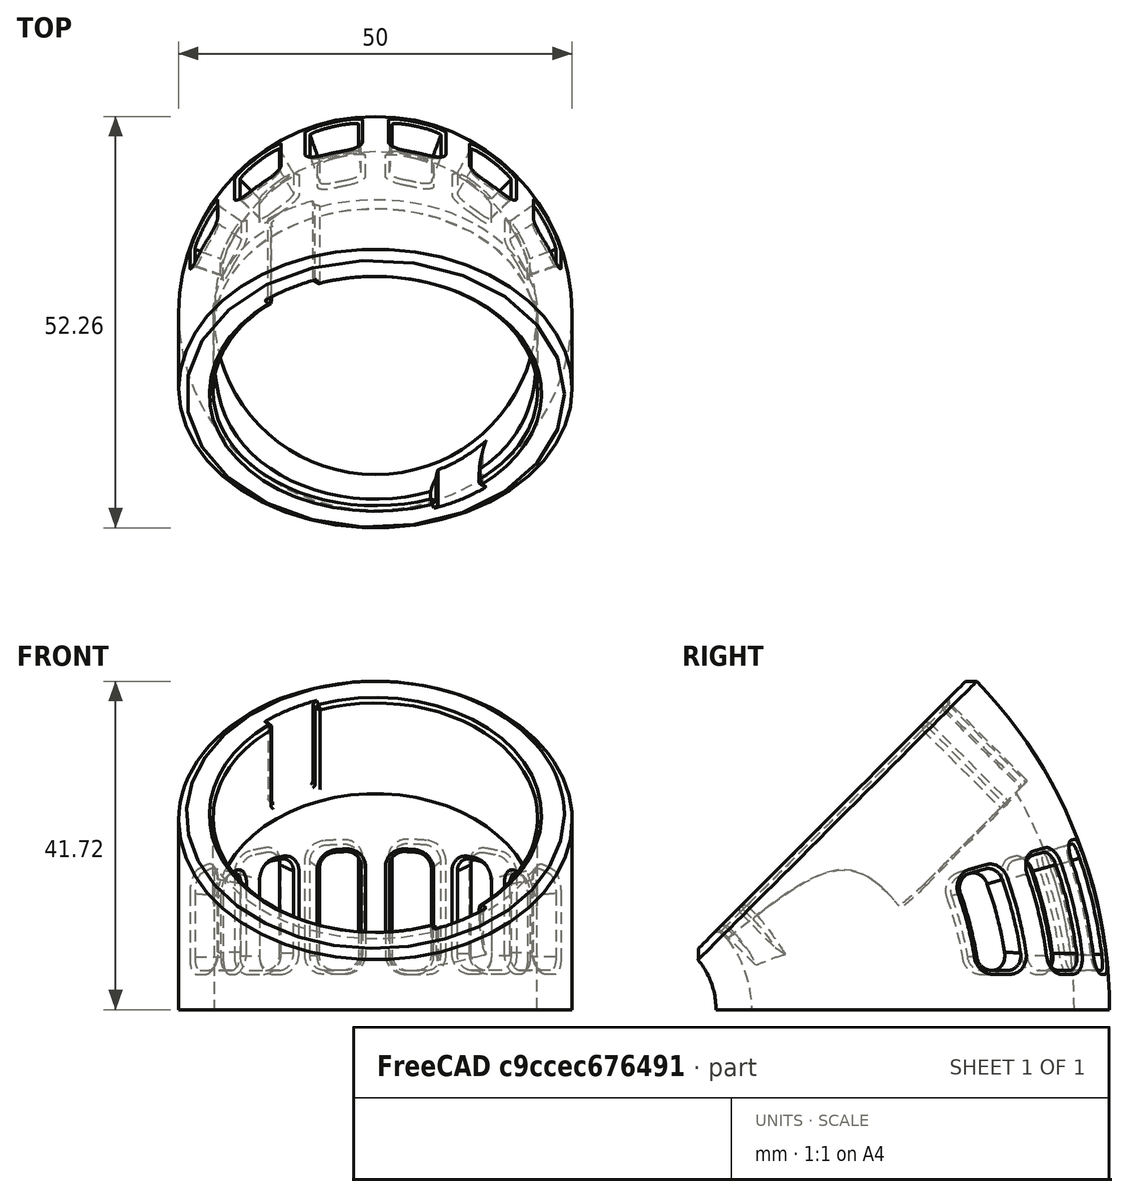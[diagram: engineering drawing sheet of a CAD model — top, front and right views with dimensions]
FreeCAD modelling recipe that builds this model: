
FCSTD DOCUMENT  (FreeCAD 0.19R18219 (Git))
Label: Hygrometerhalter-2
License: All rights reserved
LicenseURL: http://de.wikipedia.org/wiki/Alle_Rechte_vorbehalten
objects: Sketcher::SketchObject×3, PartDesign::Chamfer×3, PartDesign::Fillet×2, PartDesign::Line×1, PartDesign::Revolution×1, PartDesign::Pocket×1, PartDesign::Groove×1, PartDesign::Mirrored×1, PartDesign::Body×1, Mesh::Feature×1
note: 17 computed .brp shape members not serialized (recipe doc carries the construction recipe); baked Part::Feature solids carry a one-line shape summary decoded from their .brp

FEATURE [Sketcher::SketchObject] Sketch
  MapMode = 5
  Support = -> [XY_Plane]
  expr: Constraints[3] = 41mm
  sketch-geometry (2):
    g0: Circle CenterX=0 CenterY=0 CenterZ=0 NormalX=0 NormalY=0 NormalZ=1 AngleXU=0 Radius=25
    g1: Circle CenterX=0 CenterY=0 CenterZ=0 NormalX=0 NormalY=0 NormalZ=1 AngleXU=0 Radius=20.5
  constraints (4):
    c: Coincident(g0,g-1)
    c: Diameter(g0) = 50  'diameter'
    c: Coincident(g1,g0)
    c: Diameter(g1) = 41
FEATURE [PartDesign::Line] DatumLine
  AttacherType = Attacher::AttachEngineLine
  AttachmentOffset = pos=(-35,0,0) rot=(0,0,1;0rad)
  MapMode = 29
  Placement = pos=(0,-35,0) rot=(0.57735,0.57735,0.57735;2.0944rad)
  Support = -> [X_Axis]
FEATURE [PartDesign::Revolution] Revolution  label="Grundkörper"
  Angle = 45
  Axis = (1,0,0)
  Base = (0,-35,0)
  Profile = -> Sketch
  ReferenceAxis = -> DatumLine
  Refine = true
FEATURE [Sketcher::SketchObject] Sketch001
  ExternalGeometry = -> [Revolution]
  MapMode = 5
  Placement = pos=(0,-17.5,17.5) rot=(1,0,0;0.785398rad)
  Support = -> [Revolution]
  sketch-geometry (9):
    g0: ArcOfCircle CenterX=0 CenterY=10.2513 CenterZ=0 NormalX=0 NormalY=0 NormalZ=1 AngleXU=0 Radius=20.6 StartAngle=5.3876 EndAngle=8.22597
    g1: ArcOfCircle CenterX=0 CenterY=10.2513 CenterZ=0 NormalX=0 NormalY=0 NormalZ=1 AngleXU=0 Radius=20.6 StartAngle=2.246 EndAngle=5.08438
    g2: LineSegment StartX=-7.48746 StartY=29.4424 StartZ=0 EndX=-7.9418 EndY=30.6069 EndZ=0
    g3: ArcOfCircle CenterX=0 CenterY=10.2513 CenterZ=0 NormalX=0 NormalY=0 NormalZ=1 AngleXU=0 Radius=21.85 StartAngle=1.94279 EndAngle=2.246
    g4: LineSegment StartX=-13.6576 StartY=27.3069 StartZ=0 EndX=-12.8762 EndY=26.3311 EndZ=0
    g5: LineSegment StartX=12.8762 StartY=-5.82861 StartZ=0 EndX=13.6576 EndY=-6.80433 EndZ=0
    g6: LineSegment StartX=7.48746 StartY=-8.93983 StartZ=0 EndX=7.9418 EndY=-10.1043 EndZ=0
    g7: ArcOfCircle CenterX=0 CenterY=10.2513 CenterZ=0 NormalX=0 NormalY=0 NormalZ=1 AngleXU=0 Radius=21.85 StartAngle=5.08438 EndAngle=5.3876
    g8: LineSegment [constr] StartX=0 StartY=10.2513 StartZ=0 EndX=12.5 EndY=-11.3994 EndZ=0
  constraints (26):
    c: Diameter(g0) = 41.2
    c: Coincident(g2,g3)
    c: Coincident(g4,g3)
    c: Coincident(g4,g1)
    c: Perpendicular(g0,g2)
    c: Perpendicular(g1,g4)
    c: Coincident(g2,g0)
    c: Coincident(g5,g0)
    c: Coincident(g6,g1)
    c: Perpendicular(g0,g5)
    c: Perpendicular(g1,g6)
    c: Coincident(g7,g5)
    c: Coincident(g7,g6)
    c: Equal(g3,g7)
    c: Coincident(g3,g0)
    c: Coincident(g3,g1)
    c: Coincident(g3,g7)
    c: Symmetric(g0,g1,g0)
    c: Symmetric(g1,g0,g0)
    c: Coincident(g0,g-3)
    c: Distance(g2) = 1.25
    c: Distance(g2,g3) = 6.6
    c: Coincident(g8,g0)
    c: PointOnObject(g8,g-3)
    c: Angle(g-2,g8) = 0.523599
    c: Symmetric(g6,g5,g8)
FEATURE [PartDesign::Pocket] Pocket  label="Ausschnitt"
  BaseFeature = -> Revolution
  Length = 14.5
  Length2 = 100
  Profile = -> Sketch001
  Refine = true
  Type = 0
FEATURE [PartDesign::Chamfer] Chamfer  label="Außenfase"
  Base = -> Pocket [Edge3]
  BaseFeature = -> Pocket
  Size = 1
FEATURE [PartDesign::Chamfer] Chamfer001  label="Innenfase"
  Base = -> Chamfer [Edge7,Edge11,Edge10,Edge8,Edge12,Edge14,Edge30,Edge23,Edge32,Edge25]
  BaseFeature = -> Chamfer
  Size = 0.5
FEATURE [Sketcher::SketchObject] Sketch003
  AttachmentOffset = pos=(0,0,5) rot=(0,0,1;0rad)
  MapMode = 5
  Placement = pos=(0,0,5) rot=(0,0,1;0rad)
  Support = -> [XY_Plane]
  sketch-geometry (20):
    g0: Circle [constr] CenterX=0 CenterY=0 CenterZ=0 NormalX=0 NormalY=0 NormalZ=1 AngleXU=0 Radius=30
    g1: LineSegment [constr] StartX=0 StartY=0 StartZ=0 EndX=-21.2132 EndY=21.2132 EndZ=0
    g2: LineSegment [constr] StartX=0 StartY=0 StartZ=0 EndX=-15 EndY=25.9808 EndZ=0
    g3: LineSegment StartX=-21.2132 StartY=21.2132 StartZ=0 EndX=-10.6066 EndY=10.6066 EndZ=0
    g4: LineSegment StartX=-10.6066 StartY=10.6066 StartZ=0 EndX=-7.5 EndY=12.9904 EndZ=0
    g5: LineSegment StartX=-7.5 StartY=12.9904 StartZ=0 EndX=-15 EndY=25.9808 EndZ=0
    g6: LineSegment StartX=-15 StartY=25.9808 StartZ=0 EndX=-21.2132 EndY=21.2132 EndZ=0
    g7: LineSegment StartX=-10.2606 StartY=28.1908 StartZ=0 EndX=-5.1303 EndY=14.0954 EndZ=0
    g8: LineSegment StartX=-5.1303 StartY=14.0954 StartZ=0 EndX=-1.30734 EndY=14.9429 EndZ=0
    g9: LineSegment StartX=-1.30734 StartY=14.9429 StartZ=0 EndX=-2.61467 EndY=29.8858 EndZ=0
    g10: LineSegment StartX=-2.61467 StartY=29.8858 StartZ=0 EndX=-10.2606 EndY=28.1908 EndZ=0
    g11: LineSegment [constr] StartX=-10.2606 StartY=28.1908 StartZ=0 EndX=0 EndY=0 EndZ=0
    g12: LineSegment [constr] StartX=-2.61467 StartY=29.8858 StartZ=0 EndX=0 EndY=0 EndZ=0
    g13: LineSegment StartX=-24.5746 StartY=17.2073 StartZ=0 EndX=-28.1908 EndY=10.2606 EndZ=0
    g14: LineSegment StartX=-28.1908 StartY=10.2606 StartZ=0 EndX=-14.0954 EndY=5.1303 EndZ=0
    g15: LineSegment StartX=-14.0954 StartY=5.1303 StartZ=0 EndX=-12.2873 EndY=8.60365 EndZ=0
    g16: LineSegment StartX=-12.2873 StartY=8.60365 StartZ=0 EndX=-24.5746 EndY=17.2073 EndZ=0
    g17: LineSegment [constr] StartX=-24.5746 StartY=17.2073 StartZ=0 EndX=0 EndY=0 EndZ=0
    g18: LineSegment [constr] StartX=-28.1908 StartY=10.2606 StartZ=0 EndX=0 EndY=0 EndZ=0
    g19: Circle [constr] CenterX=0 CenterY=0 CenterZ=0 NormalX=0 NormalY=0 NormalZ=1 AngleXU=0 Radius=15
  constraints (52):
    c: Radius(g0) = 30
    c: Coincident(g1,g-1)
    c: PointOnObject(g1,g0)
    c: Coincident(g2,g-1)
    c: PointOnObject(g2,g0)
    c: Coincident(g0,g-1)
    c: Coincident(g1,g3)
    c: PointOnObject(g3,g1)
    c: Coincident(g3,g4)
    c: PointOnObject(g4,g2)
    c: Coincident(g4,g5)
    c: Coincident(g5,g2)
    c: Coincident(g5,g6)
    c: Coincident(g6,g3)
    c: Angle(g2,g1) = 0.261799
    c: PointOnObject(g7,g0)
    c: Coincident(g7,g8)
    c: Coincident(g8,g9)
    c: PointOnObject(g9,g0)
    c: Coincident(g9,g10)
    c: Coincident(g10,g7)
    c: Coincident(g11,g7)
    c: Coincident(g11,g-1)
    c: Coincident(g12,g9)
    c: Coincident(g12,g-1)
    c: PointOnObject(g7,g11)
    c: PointOnObject(g8,g12)
    c: Angle(g-2,g12) = 0.0872665
    c: Angle(g11,g2) = 0.174533
    c: PointOnObject(g13,g0)
    c: PointOnObject(g13,g0)
    c: Coincident(g13,g14)
    c: Coincident(g14,g15)
    c: Coincident(g15,g16)
    c: Coincident(g16,g13)
    c: Equal(g10,g6)
    c: Equal(g6,g13)
    c: Coincident(g17,g13)
    c: Coincident(g17,g-1)
    c: Coincident(g18,g13)
    c: Coincident(g18,g-1)
    c: PointOnObject(g14,g18)
    c: PointOnObject(g15,g17)
    c: Coincident(g19,g-1)
    c: Radius(g19) = 15
    c: PointOnObject(g3,g19)
    c: PointOnObject(g4,g19)
    c: PointOnObject(g7,g19)
    c: PointOnObject(g8,g19)
    c: PointOnObject(g15,g19)
    c: PointOnObject(g14,g19)
    c: Angle(g1,g17) = 0.174533
FEATURE [PartDesign::Groove] Groove  label="Lüftung"
  Angle = 16
  Axis = (1,0,0)
  Base = (0,-35,0)
  BaseFeature = -> Chamfer001
  Profile = -> Sketch003
  ReferenceAxis = -> DatumLine
  Refine = true
FEATURE [PartDesign::Mirrored] Mirrored
  BaseFeature = -> Groove
  MirrorPlane = -> YZ_Plane
  Originals = -> [Groove]
  Refine = true
FEATURE [PartDesign::Fillet] Fillet  label="Lüftung Rundung"
  Base = -> Mirrored [Edge139,Edge131,Edge135,Edge127,Edge123,Edge141,Edge133,Edge137,Edge126,Edge122,Edge132,Edge136,Edge140,Edge138,Edge130,Edge134,Edge128,Edge124,Edge129,Edge125,Edge121,Edge142,Edge143,Edge144]
  BaseFeature = -> Mirrored
  Radius = 2
FEATURE [PartDesign::Chamfer] Chamfer002  label="Lüftung Fase"
  Base = -> Fillet [Face2,Face18,Face26,Face46,Face38,Face54]
  BaseFeature = -> Fillet
  Size = 0.5
FEATURE [PartDesign::Fillet] Fillet001
  Base = -> Chamfer002 [Face15]
  BaseFeature = -> Chamfer002
  Radius = 0.3
FEATURE [PartDesign::Body] Body
  Group = -> [Sketch,DatumLine,Revolution,Sketch001,Pocket,Chamfer,Chamfer001,Sketch003,Groove,Mirrored,Fillet,Chamfer002,Fillet001]
  Origin = -> Origin
  Tip = -> Fillet001
FEATURE [Mesh::Feature] Mesh  label="Body (Meshed)"
